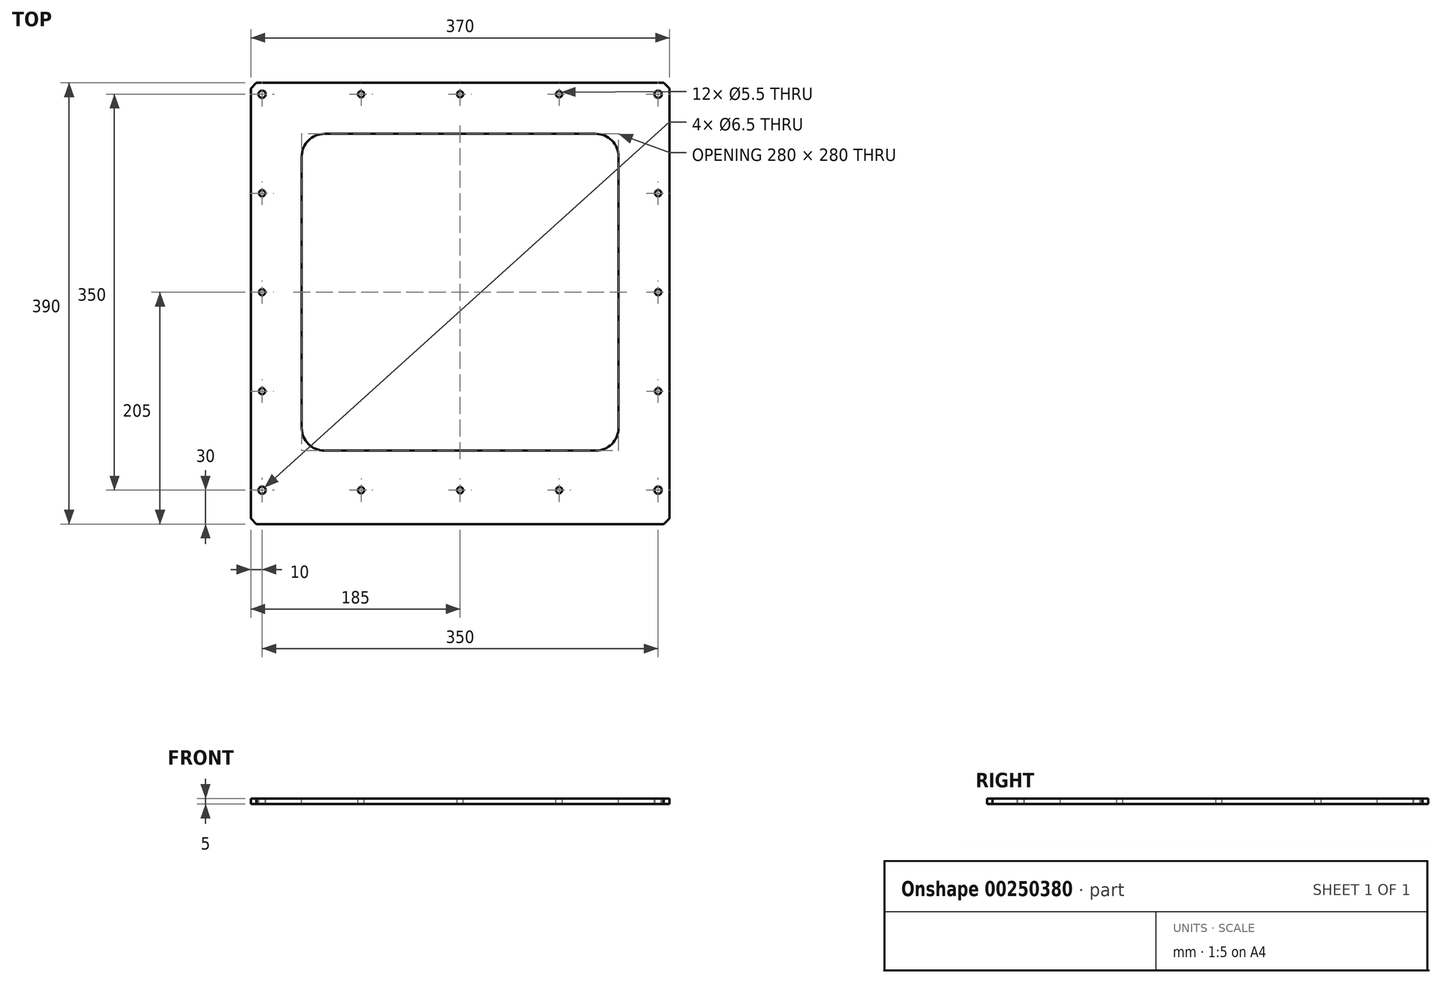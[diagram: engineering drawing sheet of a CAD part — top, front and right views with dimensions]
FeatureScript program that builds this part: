
annotation { "Feature Type Name" : "Feature", "Feature Type Description" : "" }
export const myFeature = defineFeature(function(context is Context, id is Id, definition is map)
    precondition{}
    {
        {
            var Q0;
            Q0=qCreatedBy(makeId("Top.planeOp"),FACE);
            var sketch = newSketch(context, id + "F0", { "sketchPlane" : qUnion([Q0])});
            skLineSegment(sketch, "E0.bottom", {"start": v(-175, 175) * mm, "end": v(175, 175) * mm, "construction": true});
            skLineSegment(sketch, "E0.top", {"start": v(-175, -175) * mm, "end": v(175, -175) * mm, "construction": true});
            skLineSegment(sketch, "E0.left", {"start": v(-175, 175) * mm, "end": v(-175, -175) * mm, "construction": true});
            skLineSegment(sketch, "E0.right", {"start": v(175, 175) * mm, "end": v(175, -175) * mm, "construction": true});
            skPoint(sketch, "E1", {"position": v(-175, -175) * mm});
            skPoint(sketch, "E2", {"position": v(-175, 175) * mm});
            skPoint(sketch, "E3.1.0.0", {"position": v(-87.5, -175) * mm});
            skPoint(sketch, "E3.1.1.0", {"position": v(-87.5, 175) * mm});
            skPoint(sketch, "E3.2.0.0", {"position": v(0, -175) * mm});
            skPoint(sketch, "E3.2.1.0", {"position": v(0, 175) * mm});
            skPoint(sketch, "E3.3.0.0", {"position": v(87.5, -175) * mm});
            skPoint(sketch, "E3.3.1.0", {"position": v(87.5, 175) * mm});
            skLineSegment(sketch, "E3.direction1", {"start": v(-175, -175) * mm, "end": v(-87.5, -175) * mm, "construction": true});
            skLineSegment(sketch, "E3.direction2", {"start": v(-175, -175) * mm, "end": v(-175, 175) * mm, "construction": true});
            skPoint(sketch, "E4.0.1.0", {"position": v(-175, -87.5) * mm});
            skPoint(sketch, "E4.0.2.0", {"position": v(-175, 0) * mm});
            skPoint(sketch, "E4.0.3.0", {"position": v(-175, 87.5) * mm});
            skPoint(sketch, "E4.1.0.0", {"position": v(175, -175) * mm});
            skPoint(sketch, "E4.1.1.0", {"position": v(175, -87.5) * mm});
            skPoint(sketch, "E4.1.2.0", {"position": v(175, 0) * mm});
            skPoint(sketch, "E4.1.3.0", {"position": v(175, 87.5) * mm});
            skLineSegment(sketch, "E4.direction2", {"start": v(-175, -175) * mm, "end": v(-175, -87.5) * mm, "construction": true});
            skLineSegment(sketch, "E5.bottom", {"start": v(-185, 185) * mm, "end": v(185, 185) * mm});
            skLineSegment(sketch, "E5.top", {"start": v(-185, -205) * mm, "end": v(185, -205) * mm});
            skLineSegment(sketch, "E5.left", {"start": v(-185, 185) * mm, "end": v(-185, -205) * mm});
            skLineSegment(sketch, "E5.right", {"start": v(185, 185) * mm, "end": v(185, -205) * mm});
            skLineSegment(sketch, "E6.bottom", {"start": v(-120, 140) * mm, "end": v(120, 140) * mm});
            skLineSegment(sketch, "E6.top", {"start": v(-120, -140) * mm, "end": v(120, -140) * mm});
            skLineSegment(sketch, "E6.left", {"start": v(-140, 120) * mm, "end": v(-140, -120) * mm});
            skLineSegment(sketch, "E6.right", {"start": v(140, 120) * mm, "end": v(140, -120) * mm});
            skPoint(sketch, "E7.visualSharp", {"position": v(-140, 140) * mm});
            skArc(sketch, "E7.filletArc", {"start": v(-120, 140) * mm, "mid": v(-134.14, 134.14) * mm, "end": v(-140, 120) * mm});
            skPoint(sketch, "E8.visualSharp", {"position": v(-140, -140) * mm});
            skArc(sketch, "E8.filletArc", {"start": v(-140, -120) * mm, "mid": v(-134.14, -134.14) * mm, "end": v(-120, -140) * mm});
            skPoint(sketch, "E9.visualSharp", {"position": v(140, -140) * mm});
            skArc(sketch, "E9.filletArc", {"start": v(120, -140) * mm, "mid": v(134.14, -134.14) * mm, "end": v(140, -120) * mm});
            skPoint(sketch, "E10.visualSharp", {"position": v(140, 140) * mm});
            skArc(sketch, "E10.filletArc", {"start": v(140, 120) * mm, "mid": v(134.14, 134.14) * mm, "end": v(120, 140) * mm});
            skSolve(sketch);
        }
        {
            var Q0;
            Q0=makeQuery(id+"F0.imprint","IMPRINT",FACE,{"disambiguationData":[TD([[makeQuery(id+"F0.imprint","IMPRINT",EDGE,{"derivedFrom":sQuery(id+"F0.wireOp",EDGE,"E5.bottom")}),-1.0]])]});
            extrude(context, id + "F1", {"entities" : qUnion([Q0]), "oppositeDirection" : true, "depth" : 5 * mm});
        }
        {
            var Q0;
            Q0=sQuery(id+"F0.wireOp",VERTEX,"E4.0.3.0");
            var Q1;
            Q1=sQuery(id+"F0.wireOp",VERTEX,"E4.0.2.0");
            var Q2;
            Q2=sQuery(id+"F0.wireOp",VERTEX,"E4.0.1.0");
            var Q3;
            Q3=sQuery(id+"F0.wireOp",VERTEX,"E3.1.0.0");
            var Q4;
            Q4=sQuery(id+"F0.wireOp",VERTEX,"E3.2.0.0");
            var Q5;
            Q5=sQuery(id+"F0.wireOp",VERTEX,"E3.3.0.0");
            var Q6;
            Q6=sQuery(id+"F0.wireOp",VERTEX,"E4.1.1.0");
            var Q7;
            Q7=sQuery(id+"F0.wireOp",VERTEX,"E4.1.3.0");
            var Q8;
            Q8=sQuery(id+"F0.wireOp",VERTEX,"E3.3.1.0");
            var Q9;
            Q9=sQuery(id+"F0.wireOp",VERTEX,"E3.2.1.0");
            var Q10;
            Q10=sQuery(id+"F0.wireOp",VERTEX,"E3.1.1.0");
            var Q11;
            Q11=sQuery(id+"F0.wireOp",VERTEX,"E4.1.2.0");
            var Q12;
            Q12=makeQuery(id+"F1.opExtrude","SWEPT_BODY",BODY,{"disambiguationData":[OSD([sQuery(id+"F0.wireOp",EDGE,"E5.bottom"),sQuery(id+"F0.wireOp",EDGE,"E5.top"),sQuery(id+"F0.wireOp",EDGE,"E5.left"),sQuery(id+"F0.wireOp",EDGE,"E5.right"),sQuery(id+"F0.wireOp",EDGE,"E6.bottom"),sQuery(id+"F0.wireOp",EDGE,"E6.top"),sQuery(id+"F0.wireOp",EDGE,"E6.left"),sQuery(id+"F0.wireOp",EDGE,"E6.right"),sQuery(id+"F0.wireOp",EDGE,"E7.filletArc"),sQuery(id+"F0.wireOp",EDGE,"E8.filletArc"),sQuery(id+"F0.wireOp",EDGE,"E9.filletArc"),sQuery(id+"F0.wireOp",EDGE,"E10.filletArc")])]});
            hole(context, id + "F2", {"style" : HoleStyle.SIMPLE, "endStyle" : HoleEndStyle.BLIND, "holeDiameter" : 5.5 * mm, "holeDepth" : 17 * mm, "tappedDepth" : 12 * mm, "tapClearance" : 3, "locations" : qUnion([Q0, Q1, Q2, Q3, Q4, Q5, Q6, Q7, Q8, Q9, Q10, Q11]), "scope" : qUnion([Q12])});
        }
        {
            var Q0;
            Q0=sQuery(id+"F0.wireOp",VERTEX,"E1");
            var Q1;
            Q1=sQuery(id+"F0.wireOp",VERTEX,"E2");
            var Q2;
            Q2=sQuery(id+"F0.wireOp",VERTEX,"E0.right.start");
            var Q3;
            Q3=sQuery(id+"F0.wireOp",VERTEX,"E4.1.0.0");
            var Q4;
            Q4=makeQuery(id+"F1.opExtrude","SWEPT_BODY",BODY,{"disambiguationData":[OSD([sQuery(id+"F0.wireOp",EDGE,"E5.bottom"),sQuery(id+"F0.wireOp",EDGE,"E5.top"),sQuery(id+"F0.wireOp",EDGE,"E5.left"),sQuery(id+"F0.wireOp",EDGE,"E5.right"),sQuery(id+"F0.wireOp",EDGE,"E6.bottom"),sQuery(id+"F0.wireOp",EDGE,"E6.top"),sQuery(id+"F0.wireOp",EDGE,"E6.left"),sQuery(id+"F0.wireOp",EDGE,"E6.right"),sQuery(id+"F0.wireOp",EDGE,"E7.filletArc"),sQuery(id+"F0.wireOp",EDGE,"E8.filletArc"),sQuery(id+"F0.wireOp",EDGE,"E9.filletArc"),sQuery(id+"F0.wireOp",EDGE,"E10.filletArc")])]});
            hole(context, id + "F3", {"style" : HoleStyle.SIMPLE, "endStyle" : HoleEndStyle.BLIND, "holeDiameter" : 6.5 * mm, "holeDepth" : 17 * mm, "tappedDepth" : 12 * mm, "tapClearance" : 3, "locations" : qUnion([Q0, Q1, Q2, Q3]), "scope" : qUnion([Q4])});
        }
        {
            var Q0;
            Q0=makeQuery(id+"F1.opExtrude","SWEPT_EDGE",EDGE,{"disambiguationData":[OSD([sQuery(id+"F0.wireOp",EDGE,"E5.top"),sQuery(id+"F0.wireOp",EDGE,"E5.left")])]});
            var Q1;
            Q1=makeQuery(id+"F1.opExtrude","SWEPT_EDGE",EDGE,{"disambiguationData":[OSD([sQuery(id+"F0.wireOp",EDGE,"E5.top"),sQuery(id+"F0.wireOp",EDGE,"E5.right")])]});
            var Q2;
            Q2=makeQuery(id+"F1.opExtrude","SWEPT_EDGE",EDGE,{"disambiguationData":[OSD([sQuery(id+"F0.wireOp",EDGE,"E5.bottom"),sQuery(id+"F0.wireOp",EDGE,"E5.right")])]});
            var Q3;
            Q3=makeQuery(id+"F1.opExtrude","SWEPT_EDGE",EDGE,{"disambiguationData":[OSD([sQuery(id+"F0.wireOp",EDGE,"E5.bottom"),sQuery(id+"F0.wireOp",EDGE,"E5.left")])]});
            chamfer(context, id + "F4", {"entities" : qUnion([Q0, Q1, Q2, Q3]), "width" : 5 * mm, "tangentPropagation" : true});
        }
    });
